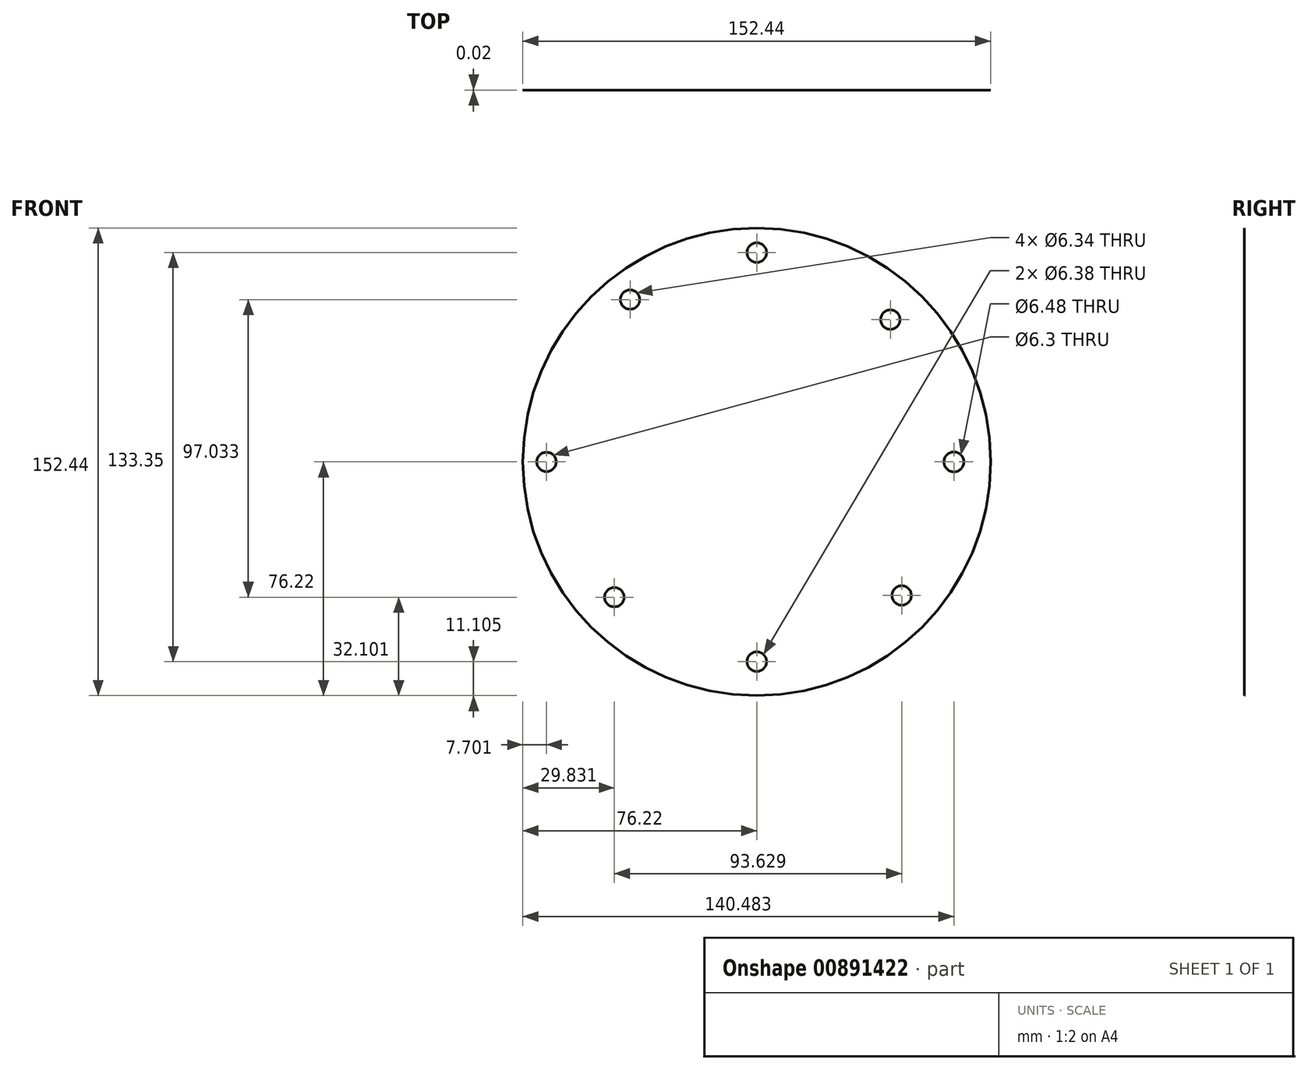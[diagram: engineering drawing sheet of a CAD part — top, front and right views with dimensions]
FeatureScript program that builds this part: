
annotation { "Feature Type Name" : "Feature", "Feature Type Description" : "" }
export const myFeature = defineFeature(function(context is Context, id is Id, definition is map)
    precondition{}
    {
        {
            var Q0;
            Q0=qCreatedBy(makeId("Front.planeOp"),FACE);
            var sketch = newSketch(context, id + "F0", { "sketchPlane" : qUnion([Q0])});
            skCircle(sketch, "E0", {"center": v(0, 0) * mm, "radius": 76.22 * mm});
            skSolve(sketch);
        }
        {
            var Q0;
            Q0 = qSketchRegion(id + "F0", true);
            extrude(context, id + "F1", {"entities" : qUnion([Q0]), "depth" : 1 / 50.8 * mm, "offsetDistance" : 25.4 * mm});
        }
        {
            var Q0;
            Q0=qCreatedBy(makeId("Front.planeOp"),FACE);
            var sketch = newSketch(context, id + "F2", { "sketchPlane" : qUnion([Q0])});
            skCircle(sketch, "E1", {"center": v(0, 68.24) * mm, "radius": 3.19 * mm});
            skCircle(sketch, "E2", {"center": v(0, -65.11) * mm, "radius": 3.19 * mm});
            skCircle(sketch, "E3", {"center": v(64.26, 0) * mm, "radius": 3.24 * mm});
            skCircle(sketch, "E4", {"center": v(-68.52, 0) * mm, "radius": 3.15 * mm});
            skCircle(sketch, "E5", {"center": v(-41.28, 52.91) * mm, "radius": 3.17 * mm});
            skCircle(sketch, "E6", {"center": v(47.24, -43.55) * mm, "radius": 3.17 * mm});
            skCircle(sketch, "E7", {"center": v(-46.39, -44.12) * mm, "radius": 3.17 * mm});
            skCircle(sketch, "E8", {"center": v(43.55, 46.39) * mm, "radius": 3.17 * mm});
            skSolve(sketch);
        }
        {
            var Q0;
            Q0 = qSketchRegion(id + "F2", true);
            extrude(context, id + "F3", {"entities" : qUnion([Q0]), "operationType" : NewBodyOperationType.REMOVE, "depth" : 25.4 * mm, "offsetDistance" : 25.4 * mm});
        }
    });
